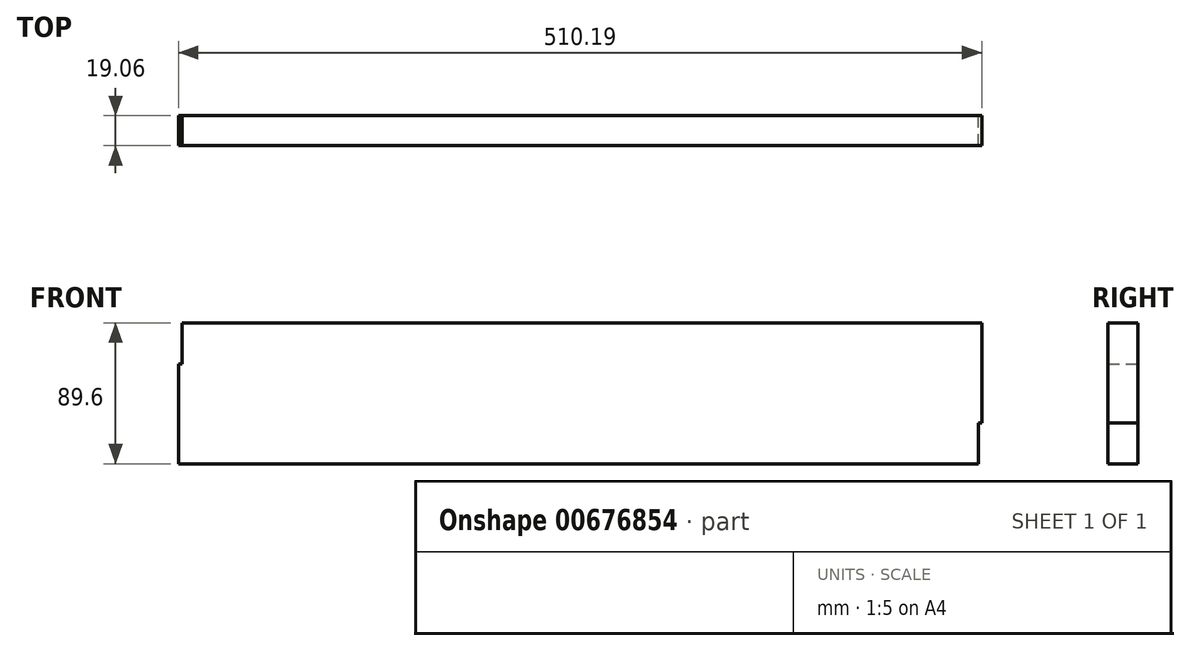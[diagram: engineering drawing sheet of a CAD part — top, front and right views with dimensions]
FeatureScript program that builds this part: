
annotation { "Feature Type Name" : "Feature", "Feature Type Description" : "" }
export const myFeature = defineFeature(function(context is Context, id is Id, definition is map)
    precondition{}
    {
        {
            var Q0;
            Q0=qCreatedBy(makeId("Front.planeOp"),FACE);
            var sketch = newSketch(context, id + "F0", { "sketchPlane" : qUnion([Q0])});
            skLineSegment(sketch, "E0.bottom", {"start": v(-256.19, 5.65) * mm, "end": v(251.81, 5.65) * mm});
            skLineSegment(sketch, "E0.top", {"start": v(-256.19, -57.85) * mm, "end": v(251.81, -57.85) * mm});
            skLineSegment(sketch, "E0.left", {"start": v(-256.19, 5.65) * mm, "end": v(-256.19, -57.85) * mm});
            skLineSegment(sketch, "E0.right", {"start": v(251.81, 5.65) * mm, "end": v(251.81, -57.85) * mm});
            skLineSegment(sketch, "E1.bottom", {"start": v(-254, 31.75) * mm, "end": v(254, 31.75) * mm});
            skLineSegment(sketch, "E1.top", {"start": v(-254, -31.75) * mm, "end": v(254, -31.75) * mm});
            skLineSegment(sketch, "E1.left", {"start": v(-254, 31.75) * mm, "end": v(-254, -31.75) * mm});
            skLineSegment(sketch, "E1.right", {"start": v(254, 31.75) * mm, "end": v(254, -31.75) * mm});
            skSolve(sketch);
        }
        {
            var Q0;
            Q0 = qSketchRegion(id + "F0", true);
            extrude(context, id + "F1", {"entities" : qUnion([Q0]), "depth" : 19.05 * mm, "offsetDistance" : 25.4 * mm, "symmetric" : true});
        }
        {
            var Q0;
            Q0=sQuery(id+"F0.wireOp",EDGE,"E1.bottom");
            var Q1;
            Q1=sQuery(id+"F0.wireOp",EDGE,"E1.top");
            var Q2;
            Q2=sQuery(id+"F0.wireOp",EDGE,"E1.left");
            var Q3;
            Q3=sQuery(id+"F0.wireOp",EDGE,"E1.right");
            extrude(context, id + "F2", {"bodyType" : ExtendedToolBodyType.SURFACE, "surfaceEntities" : qUnion([Q0, Q1, Q2, Q3]), "depth" : 19.05 * mm, "offsetDistance" : 25.4 * mm, "symmetric" : true});
        }
    });
